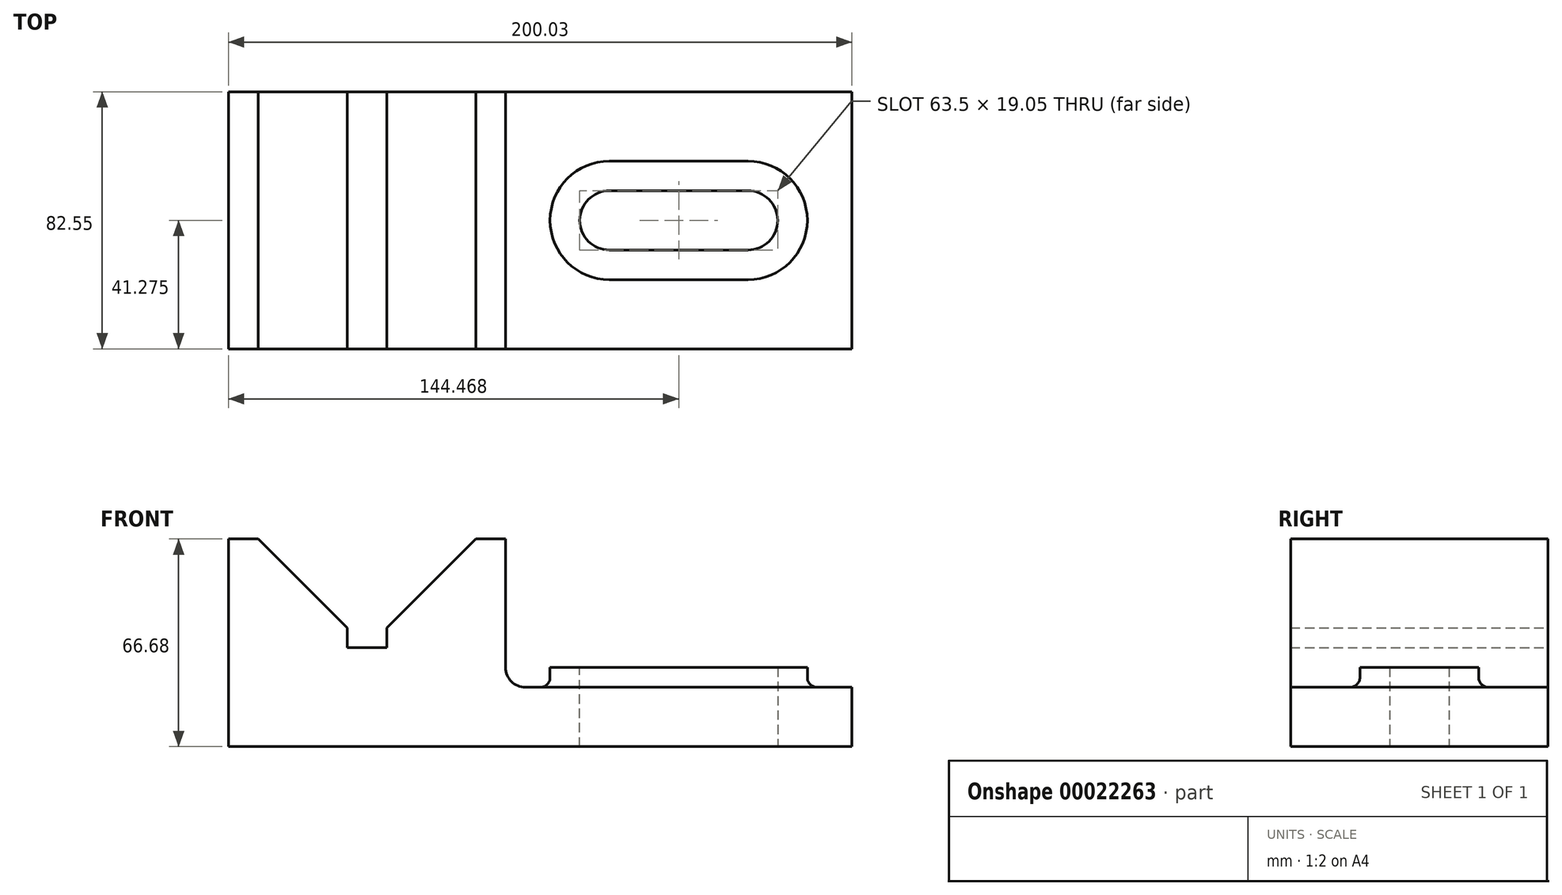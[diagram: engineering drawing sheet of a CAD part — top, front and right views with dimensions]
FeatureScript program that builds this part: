
annotation { "Feature Type Name" : "Feature", "Feature Type Description" : "" }
export const myFeature = defineFeature(function(context is Context, id is Id, definition is map)
    precondition{}
    {
        {
            var Q0;
            Q0=qCreatedBy(makeId("Front.planeOp"),FACE);
            var sketch = newSketch(context, id + "F0", { "sketchPlane" : qUnion([Q0])});
            skLineSegment(sketch, "E0.bottom", {"start": v(0, 0) * mm, "end": v(-200.03, 0) * mm});
            skLineSegment(sketch, "E0.top", {"start": v(0, 19.05) * mm, "end": v(-200.03, 19.05) * mm});
            skLineSegment(sketch, "E0.left", {"start": v(0, 0) * mm, "end": v(0, 19.05) * mm});
            skLineSegment(sketch, "E0.right", {"start": v(-200.03, 0) * mm, "end": v(-200.03, 19.05) * mm});
            skLineSegment(sketch, "E1", {"start": v(-200.03, 0) * mm, "end": v(-200.03, 66.67) * mm});
            skLineSegment(sketch, "E2", {"start": v(-200.03, 66.67) * mm, "end": v(-190.5, 66.67) * mm});
            skLineSegment(sketch, "E3", {"start": v(-190.5, 66.67) * mm, "end": v(-161.93, 38.1) * mm});
            skLineSegment(sketch, "E4", {"start": v(-161.93, 38.1) * mm, "end": v(-161.93, 31.75) * mm});
            skLineSegment(sketch, "E5", {"start": v(-161.93, 31.75) * mm, "end": v(-149.23, 31.75) * mm});
            skLineSegment(sketch, "E6", {"start": v(-149.23, 31.75) * mm, "end": v(-149.23, 38.1) * mm});
            skLineSegment(sketch, "E7", {"start": v(-149.23, 38.1) * mm, "end": v(-120.65, 66.68) * mm});
            skLineSegment(sketch, "E8", {"start": v(-120.65, 66.68) * mm, "end": v(-111.12, 66.68) * mm});
            skLineSegment(sketch, "E9", {"start": v(-111.12, 66.68) * mm, "end": v(-111.12, 19.05) * mm});
            skArc(sketch, "E10", {"start": v(-111.12, 25.4) * mm, "mid": v(-109.27, 20.9) * mm, "end": v(-104.78, 19.05) * mm});
            skSolve(sketch);
        }
        {
            var Q0;
            Q0 = qSketchRegion(id + "F0", true);
            extrude(context, id + "F1", {"entities" : qUnion([Q0]), "depth" : 82.55 * mm});
        }
        {
            var Q0;
            Q0=makeQuery(id+"F1.opExtrude","SWEPT_FACE",FACE,{"disambiguationData":[OSD([sQuery(id+"F0.wireOp",EDGE,"E0.top")])]});
            var sketch = newSketch(context, id + "F2", { "sketchPlane" : qUnion([Q0])});
            skLineSegment(sketch, "E11", {"start": v(-77.79, -60.33) * mm, "end": v(-33.34, -60.33) * mm});
            skLineSegment(sketch, "E12", {"start": v(-77.79, -22.23) * mm, "end": v(-33.34, -22.23) * mm});
            skPoint(sketch, "E13", {"position": v(-33.34, -22.23) * mm});
            skPoint(sketch, "E14", {"position": v(-33.34, -60.33) * mm});
            skLineSegment(sketch, "E15", {"start": v(-33.34, -22.23) * mm, "end": v(-33.34, -60.33) * mm});
            skPoint(sketch, "E16", {"position": v(-33.34, -41.28) * mm});
            skLineSegment(sketch, "E17", {"start": v(-33.34, -31.75) * mm, "end": v(-77.79, -31.75) * mm});
            skLineSegment(sketch, "E18", {"start": v(-77.79, -31.75) * mm, "end": v(-77.79, -22.23) * mm});
            skLineSegment(sketch, "E19", {"start": v(-33.34, -50.8) * mm, "end": v(-77.79, -50.8) * mm});
            skLineSegment(sketch, "E20", {"start": v(-77.79, -50.8) * mm, "end": v(-77.79, -60.33) * mm});
            skCircle(sketch, "E21", {"center": v(-33.34, -41.28) * mm, "radius": 9.53 * mm});
            skLineSegment(sketch, "E22", {"start": v(-77.79, -22.23) * mm, "end": v(-77.79, -60.33) * mm});
            skPoint(sketch, "E23", {"position": v(-77.79, -41.28) * mm});
            skCircle(sketch, "E24", {"center": v(-77.79, -41.28) * mm, "radius": 9.52 * mm});
            skSolve(sketch);
        }
        {
            var Q0;
            {var subQ2=sQuery(id+"F2.wireOp",EDGE,"E12");Q0=makeQuery(id+"F2.imprint","IMPRINT",FACE,{"disambiguationData":[TD([[makeQuery(id+"F2.imprint","IMPRINT",EDGE,{"derivedFrom":subQ2}),-1.0]])]});}
            var Q1;
            {var subQ5=sQuery(id+"F2.wireOp",EDGE,"E11");Q1=makeQuery(id+"F2.imprint","IMPRINT",FACE,{"disambiguationData":[TD([[makeQuery(id+"F2.imprint","IMPRINT",EDGE,{"derivedFrom":subQ5}),1.0]])]});}
            extrude(context, id + "F3", {"entities" : qUnion([Q0, Q1]), "operationType" : NewBodyOperationType.ADD, "depth" : 6.35 * mm});
        }
        {
            var Q0;
            {var subQ0=sQuery(id+"F2.wireOp",EDGE,"E15");Q0=makeQuery(id+"F3.opExtrude","SWEPT_FACE",FACE,{"disambiguationData":[OSD([subQ0]),TDD([makeQuery(id+"F2.imprint","IMPRINT",EDGE,{"disambiguationData":[TD([[makeQuery(id+"F2.imprint","INTERSECT",VERTEX,{"derivedFrom":[sQuery(id+"F2.wireOp",EDGE,"E11"),subQ0]}),1.0]])],"derivedFrom":subQ0})])]});}
            var sketch = newSketch(context, id + "F4", { "sketchPlane" : qUnion([Q0])});
            skArc(sketch, "E25", {"start": v(-63.5, 19.05) * mm, "mid": v(-61.25, 19.98) * mm, "end": v(-60.33, 22.23) * mm});
            skLineSegment(sketch, "E26", {"start": v(-60.32, 25.4) * mm, "end": v(-60.32, 19.05) * mm});
            skLineSegment(sketch, "E27", {"start": v(-60.32, 25.4) * mm, "end": v(-50.8, 25.4) * mm});
            skLineSegment(sketch, "E28", {"start": v(-50.8, 25.4) * mm, "end": v(-50.8, 19.05) * mm});
            skLineSegment(sketch, "E29", {"start": v(-50.8, 19.05) * mm, "end": v(-63.5, 19.05) * mm});
            skPoint(sketch, "E30", {"position": v(-41.28, 19.05) * mm});
            skLineSegment(sketch, "E31", {"start": v(-41.28, 19.05) * mm, "end": v(-41.28, 27.66) * mm});
            skSolve(sketch);
        }
        {
            var Q0;
            Q0 = qSketchRegion(id + "F4", true);
            var Q1;
            Q1=sQuery(id+"F4.wireOp",EDGE,"E31");
            revolve(context, id + "F5", {"operationType" : NewBodyOperationType.ADD, "entities" : qUnion([Q0]), "axis" : qUnion([Q1]), "revolveType" : RevolveType.ONE_DIRECTION, "angle" : 180 * degree});
        }
        {
            var Q0;
            Q0 = qSketchRegion(id + "F4", true);
            var Q1;
            Q1=makeQuery(id+"F5.opRevolve","CAP_FACE",FACE,{"disambiguationData":[OSD([sQuery(id+"F4.wireOp",EDGE,"E25"),sQuery(id+"F4.wireOp",EDGE,"E26"),sQuery(id+"F4.wireOp",EDGE,"E27"),sQuery(id+"F4.wireOp",EDGE,"E28"),sQuery(id+"F4.wireOp",EDGE,"E29")])],"isStart":false});
            extrude(context, id + "F6", {"entities" : qUnion([Q0, Q1]), "operationType" : NewBodyOperationType.ADD, "oppositeDirection" : true, "depth" : 44.45 * mm});
        }
        {
            var Q0;
            {var subQ0=sQuery(id+"F2.wireOp",EDGE,"E22");var subQ1=sQuery(id+"F4.wireOp",EDGE,"E25");var subQ2=sQuery(id+"F4.wireOp",EDGE,"E26");var subQ3=sQuery(id+"F4.wireOp",EDGE,"E27");var subQ4=sQuery(id+"F4.wireOp",EDGE,"E28");var subQ5=sQuery(id+"F4.wireOp",EDGE,"E29");var subQ6=makeQuery(id+"F4.imprint","INTERSECT",VERTEX,{"derivedFrom":[subQ2,subQ5]});Q0=makeQuery(id+"F6.boolean.opBoolean","MERGE",FACE,{"derivedFrom":[makeQuery(id+"F3.opExtrude","SWEPT_FACE",FACE,{"disambiguationData":[OSD([subQ0]),TDD([makeQuery(id+"F2.imprint","IMPRINT",EDGE,{"disambiguationData":[TD([[makeQuery(id+"F2.imprint","INTERSECT",VERTEX,{"derivedFrom":[sQuery(id+"F2.wireOp",EDGE,"E11"),subQ0]}),1.0]])],"derivedFrom":subQ0})])]}),makeQuery(id+"F6.opExtrude","CAP_FACE",FACE,{"disambiguationData":[OSD([subQ1,subQ2,subQ3,subQ4,subQ5]),TDD([makeQuery(id+"F4.imprint","IMPRINT",EDGE,{"derivedFrom":subQ1}),makeQuery(id+"F4.imprint","IMPRINT",EDGE,{"disambiguationData":[TD([[makeQuery(id+"F4.imprint","INTERSECT",VERTEX,{"derivedFrom":[subQ2,subQ3]}),-1.0]])],"derivedFrom":subQ2}),makeQuery(id+"F4.imprint","IMPRINT",EDGE,{"derivedFrom":subQ3}),makeQuery(id+"F4.imprint","IMPRINT",EDGE,{"derivedFrom":subQ4}),makeQuery(id+"F4.imprint","IMPRINT",EDGE,{"disambiguationData":[TD([[subQ6,-1.0]])],"derivedFrom":subQ5}),makeQuery(id+"F4.imprint","IMPRINT",EDGE,{"disambiguationData":[TD([[subQ6,1.0]])],"derivedFrom":subQ5})])],"isStart":false})]});}
            var sketch = newSketch(context, id + "F7", { "sketchPlane" : qUnion([Q0])});
            skLineSegment(sketch, "E32", {"start": v(50.8, 25.4) * mm, "end": v(60.32, 25.4) * mm});
            skLineSegment(sketch, "E33", {"start": v(60.32, 25.4) * mm, "end": v(60.32, 22.23) * mm});
            skLineSegment(sketch, "E34", {"start": v(50.8, 25.4) * mm, "end": v(50.8, 19.05) * mm});
            skLineSegment(sketch, "E35", {"start": v(50.8, 19.05) * mm, "end": v(63.5, 19.05) * mm});
            skArc(sketch, "E36", {"start": v(60.32, 22.23) * mm, "mid": v(61.25, 19.98) * mm, "end": v(63.5, 19.05) * mm});
            skPoint(sketch, "E37", {"position": v(41.27, 19.05) * mm});
            skLineSegment(sketch, "E38", {"start": v(41.27, 19.05) * mm, "end": v(41.27, 29.66) * mm});
            skSolve(sketch);
        }
        {
            var Q0;
            Q0 = qSketchRegion(id + "F7", true);
            var Q1;
            Q1=sQuery(id+"F7.wireOp",EDGE,"E38");
            revolve(context, id + "F8", {"operationType" : NewBodyOperationType.ADD, "entities" : qUnion([Q0]), "axis" : qUnion([Q1]), "revolveType" : RevolveType.ONE_DIRECTION, "oppositeDirection" : true, "angle" : 180 * degree});
        }
        {
            var Q0;
            Q0=makeQuery(id+"F8.boolean.opBoolean","SPLIT",FACE,{"disambiguationData":[TD([makeQuery(id+"F3.opExtrude","SWEPT_FACE",FACE,{"disambiguationData":[OSD([sQuery(id+"F2.wireOp",EDGE,"E17")])]})])],"derivedFrom":makeQuery(id+"F1.opExtrude","SWEPT_FACE",FACE,{"disambiguationData":[OSD([sQuery(id+"F0.wireOp",EDGE,"E0.top")])]})});
            var sketch = newSketch(context, id + "F9", { "sketchPlane" : qUnion([Q0])});
            skArc(sketch, "E39", {"start": v(-77.79, -31.75) * mm, "mid": v(-87.31, -41.28) * mm, "end": v(-77.79, -50.8) * mm});
            skArc(sketch, "E40", {"start": v(-33.34, -50.8) * mm, "mid": v(-23.81, -41.28) * mm, "end": v(-33.34, -31.75) * mm});
            skLineSegment(sketch, "E41", {"start": v(-77.79, -31.75) * mm, "end": v(-33.34, -31.75) * mm});
            skLineSegment(sketch, "E42", {"start": v(-77.79, -50.8) * mm, "end": v(-33.34, -50.8) * mm});
            skSolve(sketch);
        }
        {
            var Q0;
            Q0 = qSketchRegion(id + "F9", true);
            extrude(context, id + "F10", {"entities" : qUnion([Q0]), "operationType" : NewBodyOperationType.REMOVE, "oppositeDirection" : true, "depth" : 19.05 * mm});
        }
    });
